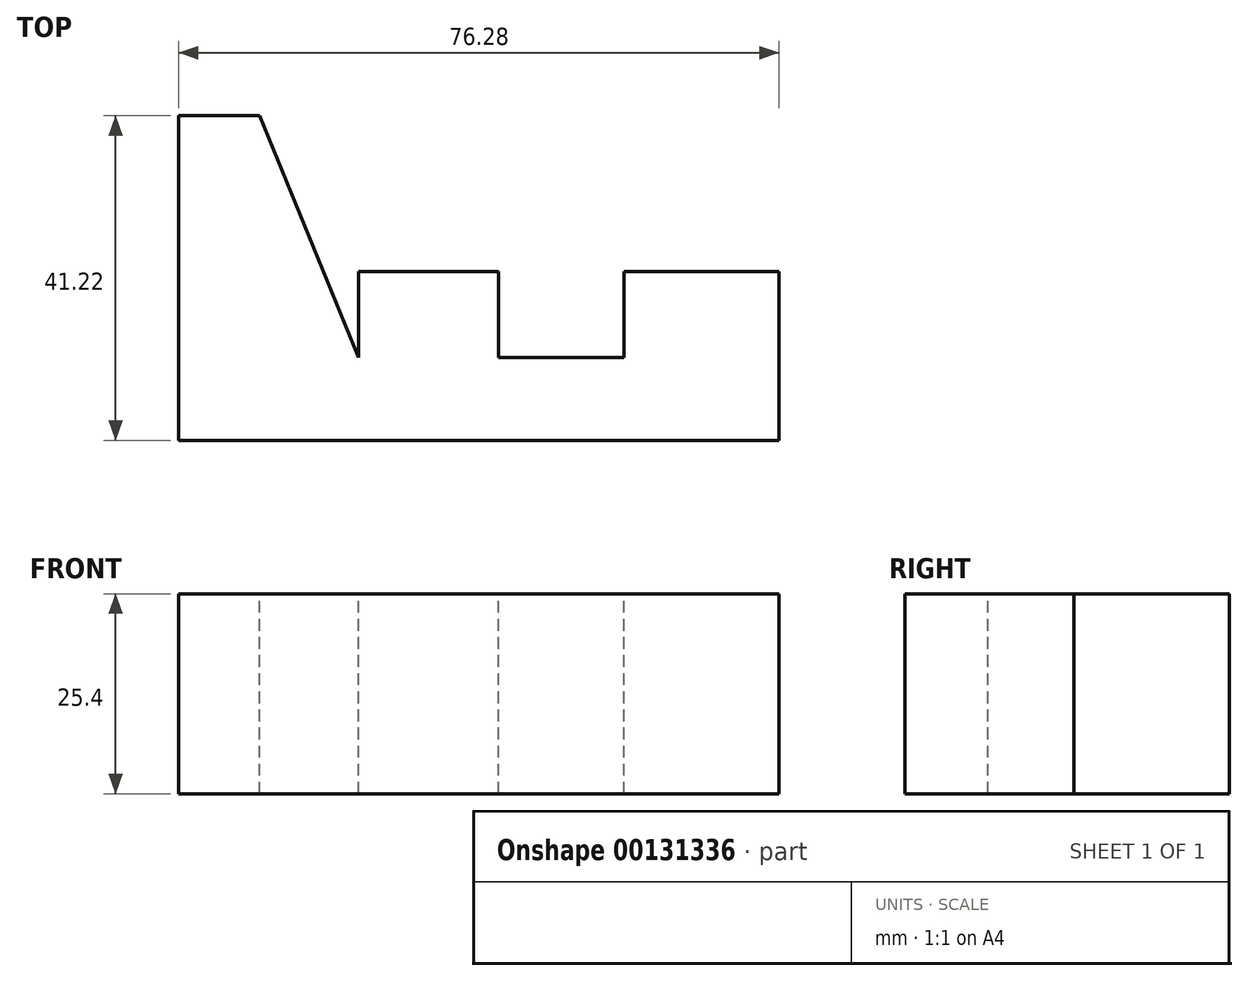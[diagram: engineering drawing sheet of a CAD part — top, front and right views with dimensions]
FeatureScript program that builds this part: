
annotation { "Feature Type Name" : "Feature", "Feature Type Description" : "" }
export const myFeature = defineFeature(function(context is Context, id is Id, definition is map)
    precondition{}
    {
        {
            var Q0;
            Q0=qCreatedBy(makeId("Top.planeOp"),FACE);
            var sketch = newSketch(context, id + "F0", { "sketchPlane" : qUnion([Q0])});
            skLineSegment(sketch, "E0", {"start": v(39.65, -18.15) * mm, "end": v(39.65, 3.27) * mm});
            skLineSegment(sketch, "E1", {"start": v(19.95, 3.27) * mm, "end": v(19.95, -7.64) * mm});
            skLineSegment(sketch, "E2", {"start": v(19.95, -7.64) * mm, "end": v(3.99, -7.64) * mm});
            skLineSegment(sketch, "E3", {"start": v(3.99, -7.64) * mm, "end": v(3.99, 3.27) * mm});
            skLineSegment(sketch, "E4", {"start": v(3.99, 3.27) * mm, "end": v(-13.8, 3.27) * mm});
            skLineSegment(sketch, "E5", {"start": v(-13.8, 3.27) * mm, "end": v(-13.8, -7.64) * mm});
            skLineSegment(sketch, "E6", {"start": v(-13.8, -7.64) * mm, "end": v(-26.32, 23.07) * mm});
            skLineSegment(sketch, "E7", {"start": v(-26.32, 23.07) * mm, "end": v(-36.63, 23.07) * mm});
            skLineSegment(sketch, "E8", {"start": v(-36.63, 23.07) * mm, "end": v(-36.63, -18.15) * mm});
            skLineSegment(sketch, "E9", {"start": v(-36.63, -18.15) * mm, "end": v(39.65, -18.15) * mm});
            skLineSegment(sketch, "E10", {"start": v(19.95, 3.27) * mm, "end": v(39.65, 3.27) * mm});
            skSolve(sketch);
        }
        {
            var Q0;
            Q0=sQuery(id+"F0.wireOp",EDGE,"E0");
            var Q1;
            Q1=sQuery(id+"F0.wireOp",EDGE,"E1");
            var Q2;
            Q2=sQuery(id+"F0.wireOp",EDGE,"E2");
            var Q3;
            Q3=sQuery(id+"F0.wireOp",EDGE,"E3");
            var Q4;
            Q4=sQuery(id+"F0.wireOp",EDGE,"E4");
            var Q5;
            Q5=sQuery(id+"F0.wireOp",EDGE,"E5");
            var Q6;
            Q6=sQuery(id+"F0.wireOp",EDGE,"E6");
            var Q7;
            Q7=sQuery(id+"F0.wireOp",EDGE,"E7");
            var Q8;
            Q8=sQuery(id+"F0.wireOp",EDGE,"E8");
            var Q9;
            Q9=sQuery(id+"F0.wireOp",EDGE,"E9");
            var Q10;
            Q10=sQuery(id+"F0.wireOp",EDGE,"E10");
            extrude(context, id + "F1", {"bodyType" : ToolBodyType.SURFACE, "surfaceEntities" : qUnion([Q0, Q1, Q2, Q3, Q4, Q5, Q6, Q7, Q8, Q9, Q10]), "depth" : 25.4 * mm});
        }
    });
